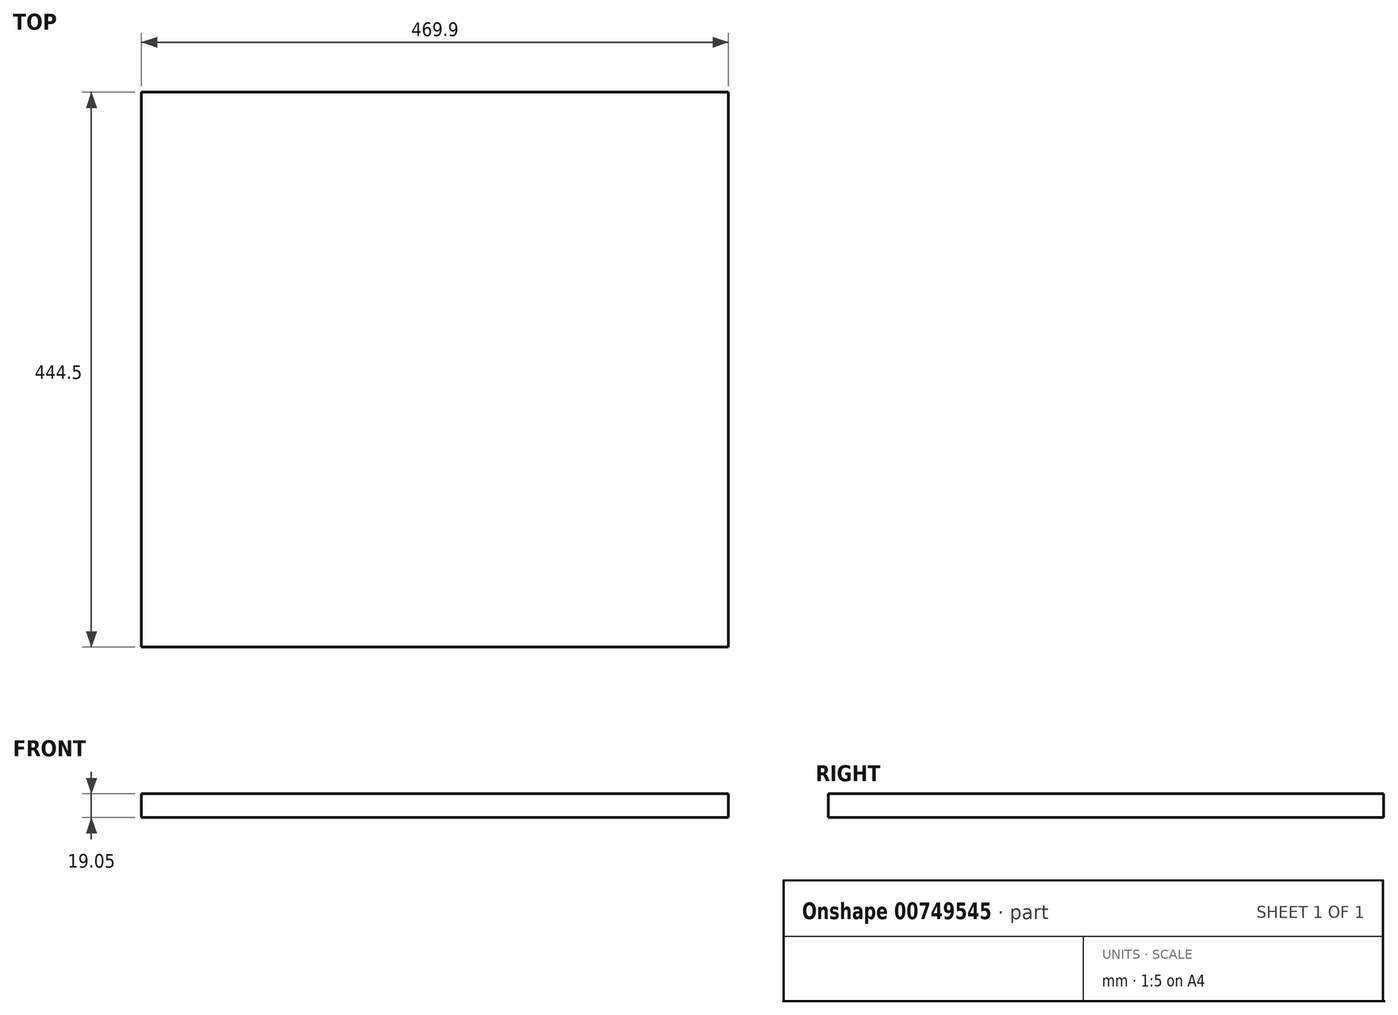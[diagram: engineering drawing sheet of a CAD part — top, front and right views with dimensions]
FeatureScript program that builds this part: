
annotation { "Feature Type Name" : "Feature", "Feature Type Description" : "" }
export const myFeature = defineFeature(function(context is Context, id is Id, definition is map)
    precondition{}
    {
        {
            var Q0;
            Q0=qCreatedBy(makeId("Top.planeOp"),FACE);
            var sketch = newSketch(context, id + "F0", { "sketchPlane" : qUnion([Q0])});
            skLineSegment(sketch, "E0.bottom", {"start": v(234.95, 222.25) * mm, "end": v(-234.95, 222.25) * mm});
            skLineSegment(sketch, "E0.top", {"start": v(234.95, -222.25) * mm, "end": v(-234.95, -222.25) * mm});
            skLineSegment(sketch, "E0.left", {"start": v(234.95, 222.25) * mm, "end": v(234.95, -222.25) * mm});
            skLineSegment(sketch, "E0.right", {"start": v(-234.95, 222.25) * mm, "end": v(-234.95, -222.25) * mm});
            skPoint(sketch, "E0.middle", {"position": v(0, 0) * mm});
            skSolve(sketch);
        }
        {
            var Q0;
            Q0=makeQuery(id+"F0.imprint","IMPRINT",FACE,{"disambiguationData":[TD([[makeQuery(id+"F0.imprint","IMPRINT",EDGE,{"derivedFrom":sQuery(id+"F0.wireOp",EDGE,"E0.bottom")}),1.0]])]});
            extrude(context, id + "F1", {"entities" : qUnion([Q0]), "depth" : 19.05 * mm, "offsetDistance" : 25.4 * mm});
        }
    });
